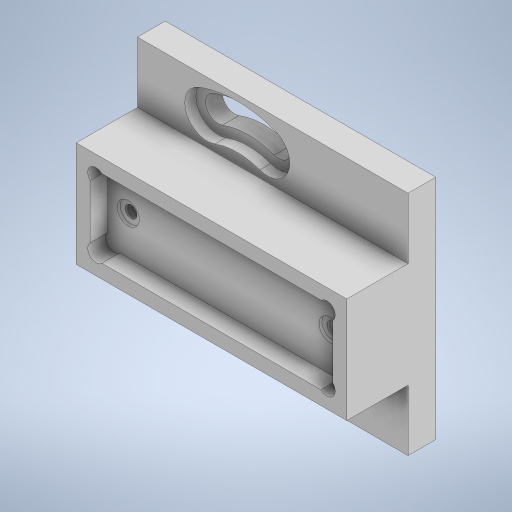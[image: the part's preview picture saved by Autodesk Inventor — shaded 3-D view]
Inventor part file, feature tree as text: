
AUTODESK INVENTOR PART (.ipt)
format: ipt  version: 2024.2 (Build 282272000, 272)  size: 486,912 bytes
history: native  units: in
note: dims shown in document units (in); Inventor stores cm internally (conversion verified against a paired STEP export)
features: extrude x9, hole x6, sketch x4, chamfer x1
ambient origin geometry x8: Origin, YZ Plane, XZ Plane, XY Plane, X Axis, Y Axis, Z Axis, Center Point
bodies: Solid1 (feature_tree)
feature tree (20):
  extrude  "Extrusion1"  TaperAngle=0.0deg  [1 undecoded]
  hole  "Hole1"  [1 undecoded]
  hole  "Hole2"  [1 undecoded]
  hole  "Hole3"  [1 undecoded]
  extrude  "Extrusion2"  TaperAngle=0.0deg  [1 undecoded]
  extrude  "Extrusion3"  Depth=0.0197in
  hole  "Hole5"  [1 undecoded]
  hole  "Hole6"  [1 undecoded]
  extrude  "Extrusion4"  Depth=0.3937in
  extrude  "Extrusion6"  Depth=0.1969in
  chamfer  "Chamfer5"  Distance=0.0413in
  sketch  "Sketch12"  dims[d2=0.5059in d3=0.0in]
  extrude  "Extrusion12"  Depth=0.0827in TaperAngle=0.0deg
  extrude  "Extrusion13"  Depth=1.9213in
  hole  "Hole7"  [1 undecoded]
  sketch  "Sketch15"  dims[d12=0.0in d13=1.4331in]
  sketch  "Sketch17"  dims[d14=0.7165in d15=0.1772in d16=0.224in d17=0.315in d18=0.3445in d19=0.5635in d20=0.3492in d21=0.0in d22=0.0in d23=0.0in d24=0.0394in d25=0.0in d26=0.0in d27=0.3937in d28=0.1969in d29=0.0413in d30=0.0827in d31=0.224in d32=0.315in d33=0.1654in d34=0.5635in d35=0.0827in d36=0.0in d37=0.0827in d38=0.0in d39=1.9213in d40=1.6142in d41=0.1969in d42=0.0in d54=0.0in d55=0.0in d56=0.0in d57=0.0in d58=0.1575in d59=0.224in d60=0.315in d61=0.0787in d62=0.5635in d63=0.0197in d64=0.0in d77=0.0394in d78=0.0413in d79=0.3937in d80=0.0in d81=0.0in d82=0.1969in d83=0.0827in d84=0.224in d85=0.315in d86=0.0787in d87=0.5635in d88=0.0827in d89=0.0in d90=0.0827in d91=0.0in d97=1.9213in d98=0.748in d99=1.7244in d100=0.5512in d101=0.126in d102=0.0in d103=0.0394in d104=0.0787in d105=45.0deg d106=0.1181in d107=45.0deg d108=45.0deg d109=45.0deg d110=0.1181in d111=0.1181in d112=0.1181in d118=0.315in d122=0.1772in d129=0.0in d130=0.0in d131=0.0787in d132=0.0in d133=0.0827in d134=0.2362in d135=0.1575in d136=0.0787in d137=90.0deg d138=0.0827in d139=0.0in d140=1.5354in d141=0.9055in d142=1.3976in d143=1.0433in d147=0.315in d148=0.1772in d149=0.1772in d150=0.315in d151=0.0in d152=0.0in d153=0.0787in d154=0.0in d127=0.0197in d128=0.0344in]
  extrude  "Extrusion14"  Depth=0.1969in TaperAngle=0.0deg
  extrude  "Extrusion15"  TaperAngle=0.0deg  [1 undecoded]
  sketch  "Sketch14"  dims[d4=0.0849in d5=0.224in d6=0.1575in d7=0.0787in d8=90.0deg d9=0.3492in d10=0.0in d11=0.0in]
note: 9 required parameter values undecoded (feature->parameter linkage not recoverable at this tier; creation-order binding heuristic only, values carry confidence <= 0.55)
